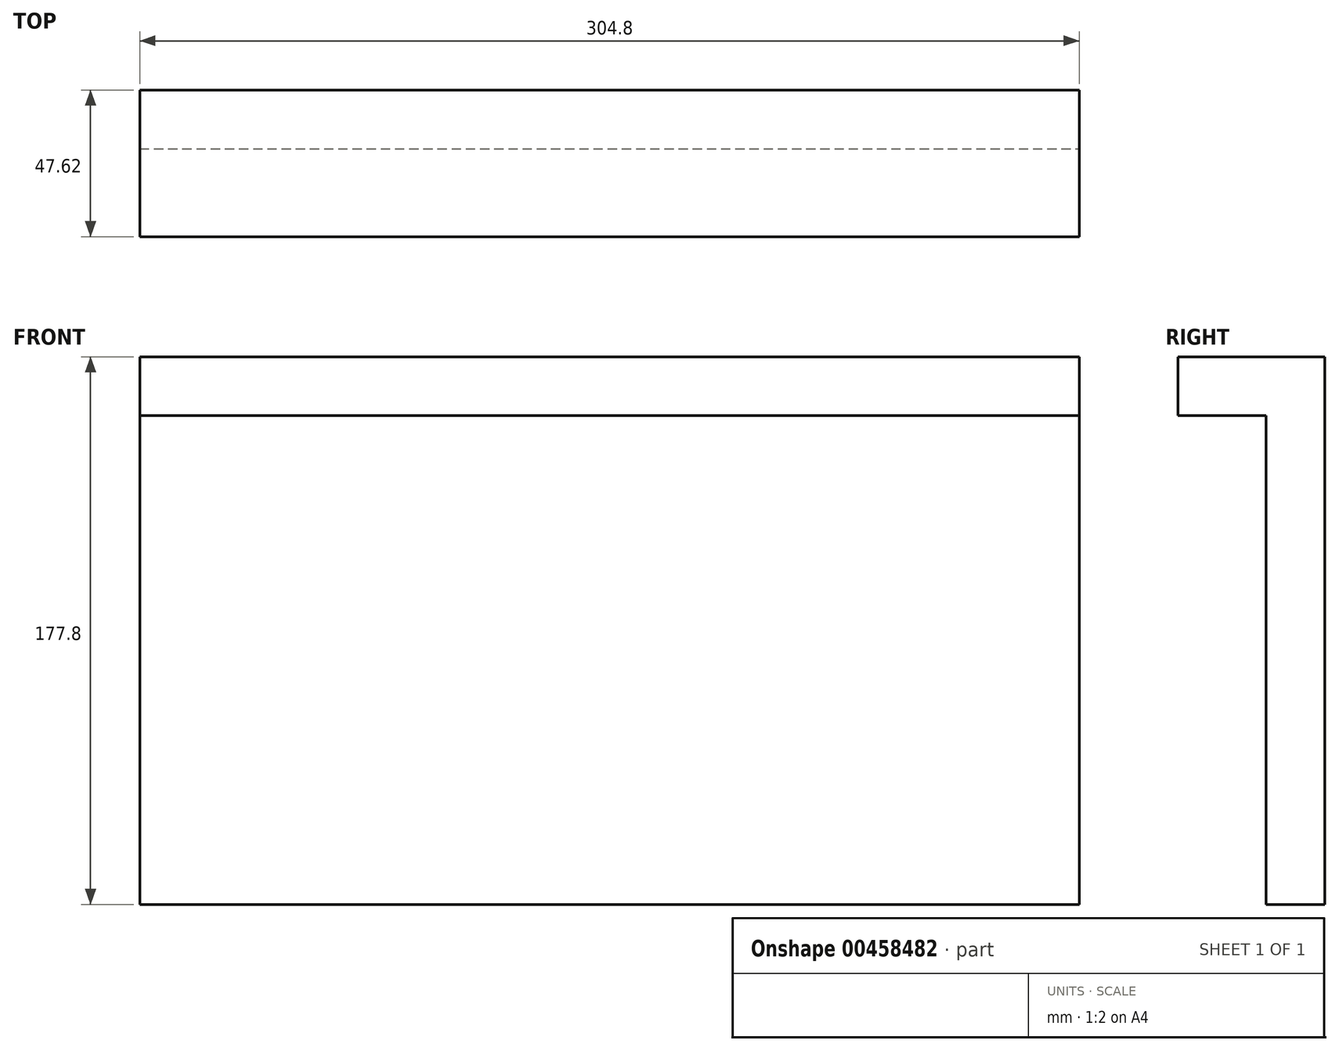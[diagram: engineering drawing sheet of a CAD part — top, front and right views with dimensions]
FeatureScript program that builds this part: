
annotation { "Feature Type Name" : "Feature", "Feature Type Description" : "" }
export const myFeature = defineFeature(function(context is Context, id is Id, definition is map)
    precondition{}
    {
        {
            var Q0;
            Q0=qCreatedBy(makeId("Front.planeOp"),FACE);
            var sketch = newSketch(context, id + "F0", { "sketchPlane" : qUnion([Q0])});
            skLineSegment(sketch, "E0", {"start": v(0, 0) * mm, "end": v(304.8, 0) * mm});
            skLineSegment(sketch, "E1", {"start": v(304.8, 0) * mm, "end": v(304.8, 177.8) * mm});
            skLineSegment(sketch, "E2", {"start": v(304.8, 177.8) * mm, "end": v(0, 177.8) * mm});
            skLineSegment(sketch, "E3", {"start": v(0, 177.8) * mm, "end": v(0, 0) * mm});
            skLineSegment(sketch, "E4.bottom", {"start": v(0, 177.8) * mm, "end": v(0, 177.8) * mm});
            skLineSegment(sketch, "E4.top", {"start": v(0, 0) * mm, "end": v(0, 0) * mm});
            skSolve(sketch);
        }
        {
            var Q0;
            Q0=makeQuery(id+"F0.imprint","IMPRINT",FACE,{"disambiguationData":[TD([[makeQuery(id+"F0.imprint","IMPRINT",EDGE,{"derivedFrom":sQuery(id+"F0.wireOp",EDGE,"E0")}),1.0]])]});
            extrude(context, id + "F1", {"entities" : qUnion([Q0]), "depth" : 19.05 * mm});
        }
        {
            var Q0;
            Q0=makeQuery(id+"F1.opExtrude","CAP_FACE",FACE,{"disambiguationData":[OSD([sQuery(id+"F0.wireOp",EDGE,"E0"),sQuery(id+"F0.wireOp",EDGE,"E1"),sQuery(id+"F0.wireOp",EDGE,"E2"),sQuery(id+"F0.wireOp",EDGE,"E3")])],"isStart":false});
            var sketch = newSketch(context, id + "F2", { "sketchPlane" : qUnion([Q0])});
            skLineSegment(sketch, "E5", {"start": v(0, 177.8) * mm, "end": v(0, 158.75) * mm});
            skLineSegment(sketch, "E6", {"start": v(0, 158.75) * mm, "end": v(304.8, 158.75) * mm});
            skLineSegment(sketch, "E7", {"start": v(304.8, 158.75) * mm, "end": v(304.8, 177.8) * mm});
            skLineSegment(sketch, "E8", {"start": v(304.8, 177.8) * mm, "end": v(0, 177.8) * mm});
            skSolve(sketch);
        }
        {
            var Q0;
            Q0=makeQuery(id+"F2.imprint","IMPRINT",FACE,{"disambiguationData":[TD([[makeQuery(id+"F2.imprint","IMPRINT",EDGE,{"derivedFrom":sQuery(id+"F2.wireOp",EDGE,"E5")}),1.0]])]});
            extrude(context, id + "F3", {"entities" : qUnion([Q0]), "operationType" : NewBodyOperationType.ADD, "depth" : 28.57 * mm});
        }
    });
